# Revit family: Windcatcher_Monodraught_X-Air Sola Boost_200
name_source: partatom
category: Mechanical Equipment
revit_build: Autodesk Revit 2014 (Build: 20130308_1515(x64)
units: mm (PartAtom-declared; Revit-internal decimal feet)

## types (2) — shared parameters
Acoustic foam = 25mm, 50mm
Actuating force = 10Nm @ nominal voltage. Running time; 150s / 95° (for volume control damper)
Actuator motors = IP54 rated
Architectural LED lighting = white / blue /green
BIMobject category = HVAC
Colours = RAL 7037 Dusty Grey / RAL 7038 Agate Grey
Date of publishing = 2015-01-05
Depth = 1540.00
Description = Natural Ventilation Roof Terminal
Design country = United Kingdom
Edition number = 2
Fire = BS 476-3:2004 / BS 476-24:1987
GRP extended colour = matched skirt (to suit roof pitch from 15 – 35 degrees)
Height = 1540 mm  [stored 5.05249 ft]
IFC Classification = Building Element Proxy
Manufacturer URL = http://www.monodraught.com
Manufacturer country = United Kingdom
Manufacturer name = Monodraught
Material 1 = Injection Moulded Luran S 757 G UV – ASA
Material 10 = Carbon sheet steel construction to BS EN
Material 11 = 10W Monocrystalline photovoltaic solar panel (LED version only)
Material 2 = Extruded Luran S 776SE UV – ASA
Material 3 = Extruded Shore A 58 Flexible Compound
Material 4 = Extruded FLUOR-ACRYL® PMMA
Material 5 = Extruded Styron CALIBRE™ 603 3 Polycarbonate
Material 6 = Extruded thermoform sheet P60R – Recycled impact Polystyrene
Material 7 = Extruded thermoform sheet P91UV – High impact Polystyrene with UV resistant capping
Material 8 = Extruded thermoform sheet  ASA200
Material 9 = 6063 Aluminium extrusion to T6 temper
Misc = Plastic_Monodraught_Windcatcher_X-Air_White
NBS Reference Code = 65-40-95-55
NBS Reference Description = Natural Ventilation Systems
Nominal height = 1440
Nominal width = 1440
Power consumption = 2W @ nominal force, 0.4W at rest, 4VA (wire sizing)
Power supply range = 19.2 – 28.8V DC. 0 – 10V
Product Guid = 6dfe068a-2be6-4870-bb36-363951bf8ddc
Product SKU = SBOOST200
Product data url = https://bimobject.com
Product family = Natural Ventilation
Product group = Natural Ventilation
QR code = http://bimobject.com
Solar Panel = Glass_Monodraught_Windcatcher_X-Air Sola Boost
UNSPSC Code = 401015
Uniclass 1.4 Code = L7535
Uniclass 1.4 Description = Natural ventilation/extraction
Uniclass 2.0 Code = SS-65-40-95-55
Uniclass 2.0 Description = Natural Ventilation Systems
Weight Net (Kg) = 164
Width = 1440 mm  [stored 4.72441 ft]
Youtube clip = https://www.youtube.com

## per-type parameters (varying)
| type | Length | Sound |
| Monodraught_Windcatcher_X-Air Sola Boost 200_Flat Roof | 1540 mm  [stored 5.05249 ft] | BS EN 20140-10:1992 |
| Monodraught_Windcatcher_X-Air Sola Boost 200_Pitched Roof | 1440 mm  [stored 4.72441 ft] | BS EN 20140-10,1992 |

note: [stored X ft] marks values corroborated as IEEE doubles in the binary element streams (Revit-internal decimal feet)

## geometry (parser evidence)
native form markers: Sweep x4
no freeform markers — native parametric forms only
